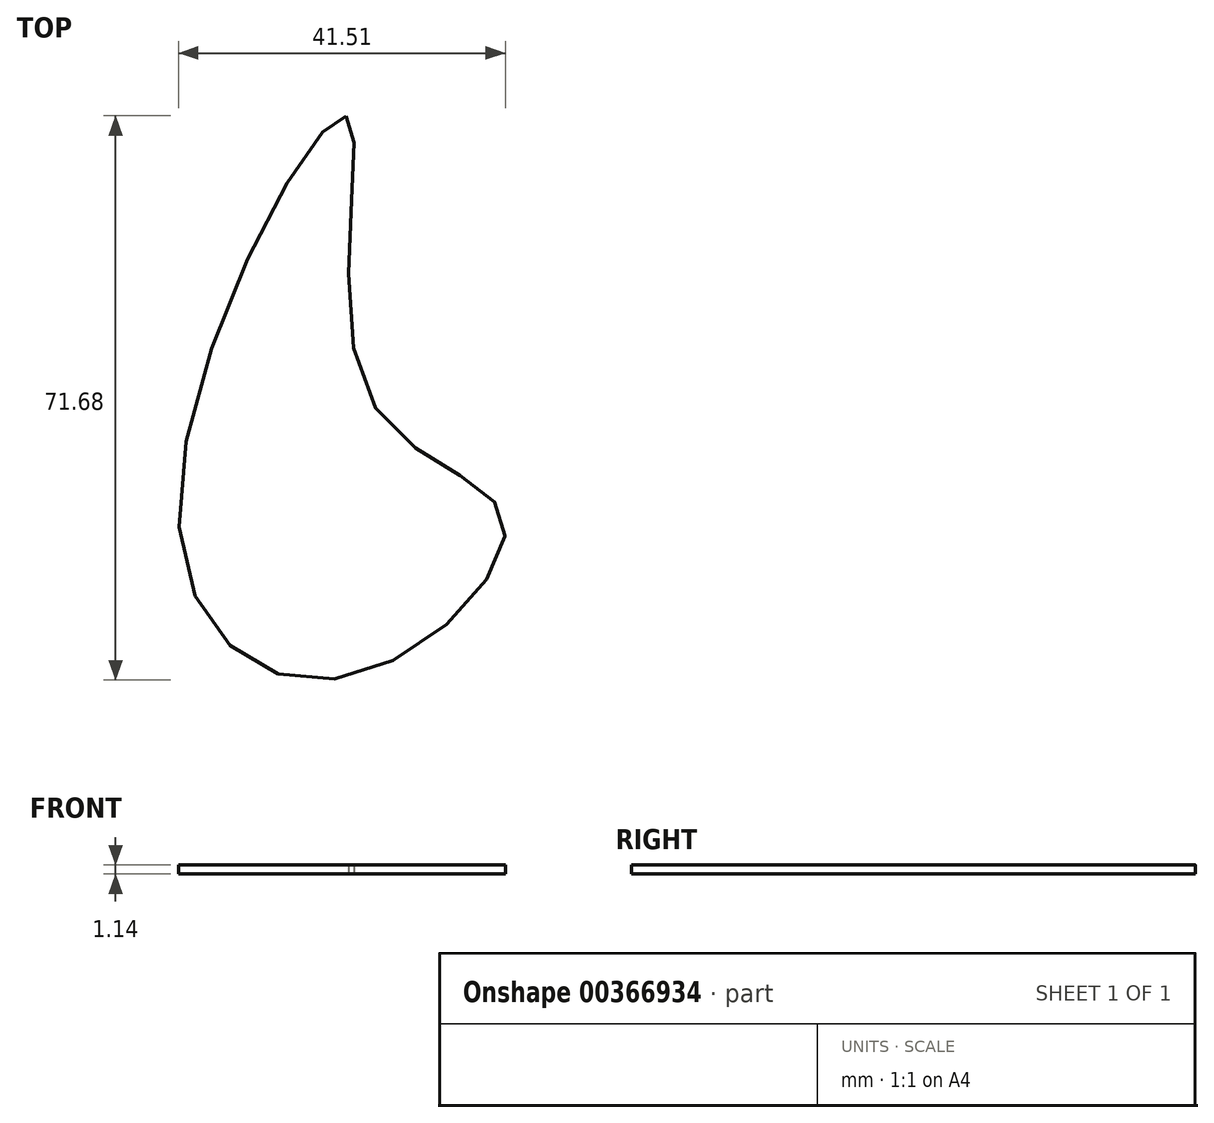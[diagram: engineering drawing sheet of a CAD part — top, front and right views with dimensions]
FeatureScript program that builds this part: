
annotation { "Feature Type Name" : "Feature", "Feature Type Description" : "" }
export const myFeature = defineFeature(function(context is Context, id is Id, definition is map)
    precondition{}
    {
        {
            var Q0;
            Q0=qCreatedBy(makeId("Top.planeOp"),FACE);
            var sketch = newSketch(context, id + "F0", { "sketchPlane" : qUnion([Q0])});
            skFitSpline(sketch, "E0", {"points": [v(0, 51.3) * mm, v(2.6, 16.16) * mm, v(20.08, 0) * mm, v(0, -19.98) * mm, v(-21.29, 0) * mm, v(0, 51.3) * mm]});
            skSolve(sketch);
        }
        {
            var Q0;
            Q0 = qSketchRegion(id + "F0", true);
            extrude(context, id + "F1", {"entities" : qUnion([Q0]), "depth" : 1.14 * mm});
        }
    });
